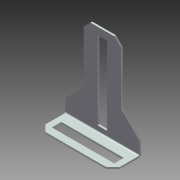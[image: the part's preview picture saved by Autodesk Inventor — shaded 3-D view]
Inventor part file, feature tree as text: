
AUTODESK INVENTOR PART (.ipt)
format: ipt  version: 2013 (Build 170138000, 138)  size: 129,536 bytes
history: native  units: mm (DEFAULTED — no unit token found)
features: sheet_metal_op x3, sketch x3, other x2, chamfer x1, extrude x1
ambient origin geometry x8: Origin, YZ Plane, XZ Plane, XY Plane, X Axis, Y Axis, Z Axis, Center Point
bodies: Solid1 (feature_tree)
feature tree (10):
  sheet_metal_op  "Face2"
  sheet_metal_op  "Flange1"
  chamfer  "Chamfer1"  Distance=3.175mm
  extrude  "Extrusion1"  Depth=3.175mm
  sketch  "Sketch1"  dims[d0=44.45mm]
  other  "Plate2"
  sketch  "Sketch2"  dims[d1=3.175mm]
  other  "Plate3"
  sheet_metal_op  "Bend1"
  sketch  "Sketch3"  dims[d2=3.175mm d3=3.175mm d4=3.175mm d6=35.56mm d7=17.78mm d8=8.89mm d9=6.985mm d10=6.985mm d11=3.556mm d12=4.572mm d13=6.604mm d14=3.429mm d15=0.8509mm d16=0.8509mm d17=0.8509mm d18=0.42545mm d19=1.7018mm d20=0.8509mm d21=12.7mm d22=90.0deg d23=0.635mm d24=3.175mm d25=3.175mm d26=45.0deg d27=2.794mm d28=2.794mm d29=3.429mm d30=4.572mm d31=25.4mm d32=0.0mm]
